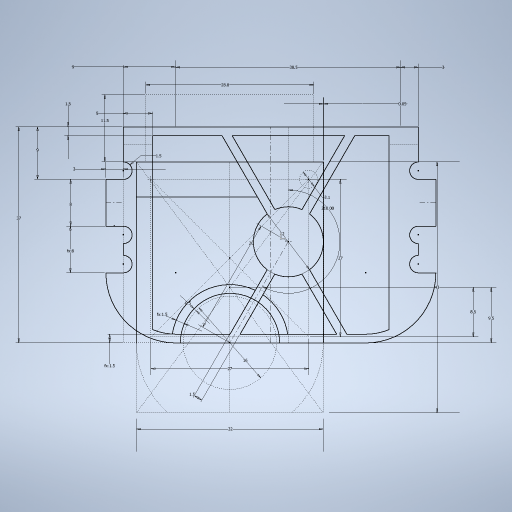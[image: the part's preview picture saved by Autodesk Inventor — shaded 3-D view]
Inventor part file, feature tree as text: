
AUTODESK INVENTOR PART (.ipt)
format: ipt  version: 2024.2 (Build 282272000, 272)  size: 317,440 bytes
history: native  units: mm
features: sketch x1
ambient origin geometry x8: Origin, YZ Plane, XZ Plane, XY Plane, X Axis, Y Axis, Z Axis, Center Point
feature tree (1):
  sketch  "Sketch1"  dims[d0=32.0mm d1=43.0mm d2=27.0mm d3=27.0mm d4=16.0mm d6=20.0mm d7=9.5mm d8=8.5mm d9=28.8mm d10=11.5mm d12=1.5mm d13=3.0mm d14=38.5mm d15=3.0mm d16=9.0mm d23=0.05mm d25=0.5mm d47=1.5mm d49=5.0mm d51=1.5mm d54=3.1mm d56=210.0deg d57=1.5mm d58=12.0mm d62=8.0mm d63=1.5mm d64=37.0mm d65=9.0mm d67=8.0mm d68=1.5mm]
